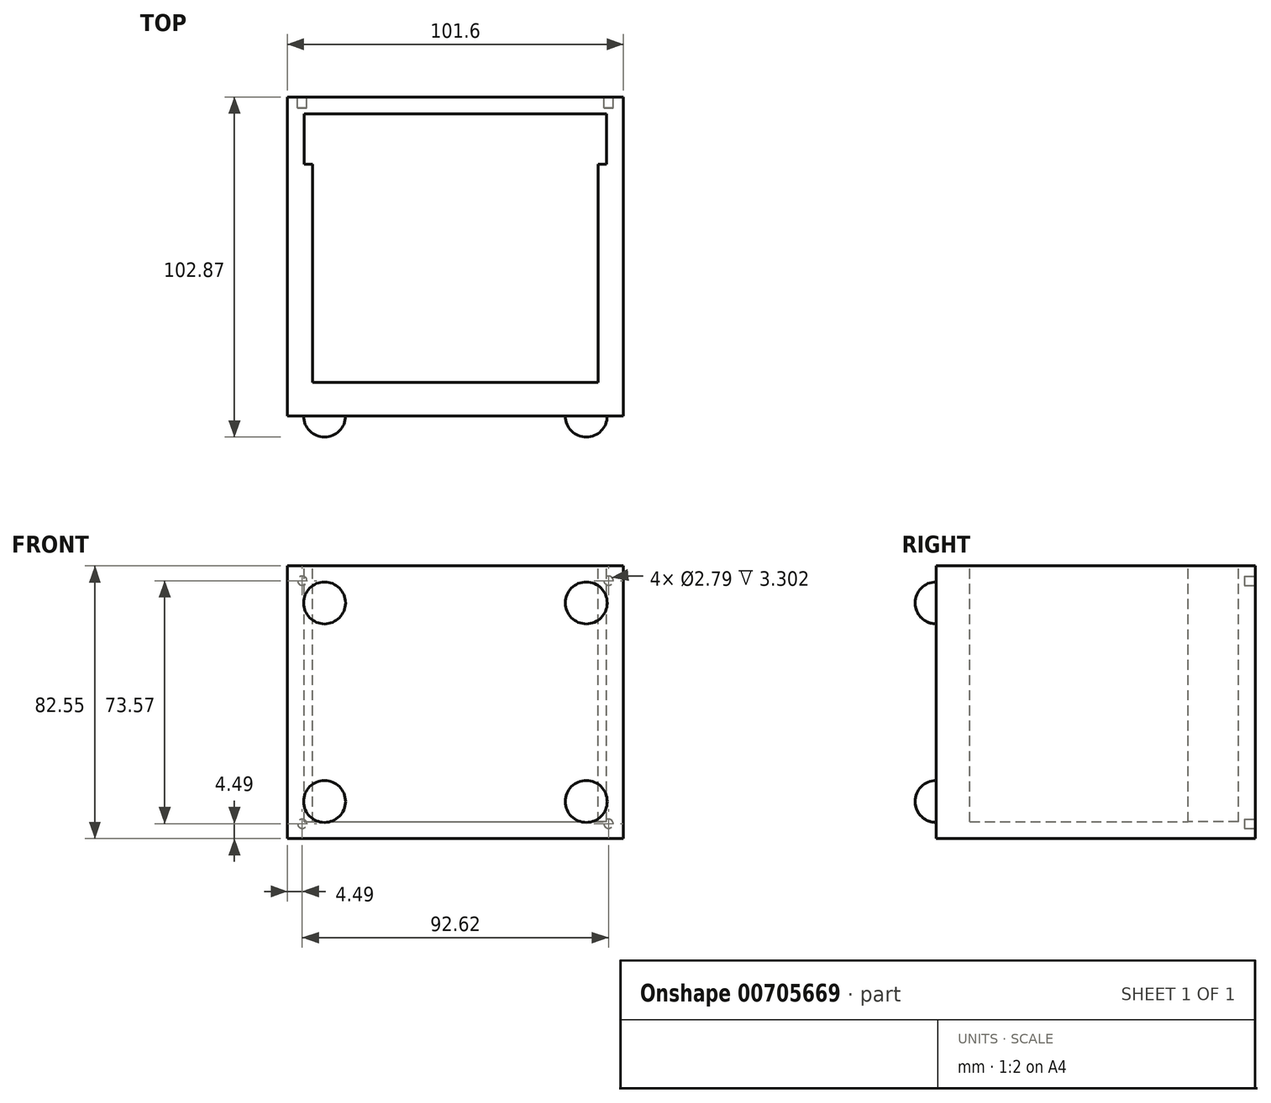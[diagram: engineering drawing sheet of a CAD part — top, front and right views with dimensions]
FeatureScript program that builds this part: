
annotation { "Feature Type Name" : "Feature", "Feature Type Description" : "" }
export const myFeature = defineFeature(function(context is Context, id is Id, definition is map)
    precondition{}
    {
        {
            var Q0;
            Q0=qCreatedBy(makeId("Top.planeOp"),FACE);
            var sketch = newSketch(context, id + "F0", { "sketchPlane" : qUnion([Q0])});
            skLineSegment(sketch, "E0.bottom", {"start": v(-50.8, 48.26) * mm, "end": v(50.8, 48.26) * mm});
            skLineSegment(sketch, "E0.top", {"start": v(-50.8, -48.26) * mm, "end": v(50.8, -48.26) * mm});
            skLineSegment(sketch, "E0.left", {"start": v(-50.8, 48.26) * mm, "end": v(-50.8, -48.26) * mm});
            skLineSegment(sketch, "E0.right", {"start": v(50.8, 48.26) * mm, "end": v(50.8, -48.26) * mm});
            skPoint(sketch, "E0.middle", {"position": v(0, 0) * mm});
            skSolve(sketch);
        }
        {
            var Q0;
            Q0 = qSketchRegion(id + "F0", true);
            extrude(context, id + "F1", {"entities" : qUnion([Q0]), "depth" : 82.55 * mm, "offsetDistance" : 25.4 * mm});
        }
        {
            var Q0;
            Q0=makeQuery(id+"F1.opExtrude","CAP_FACE",FACE,{"disambiguationData":[OSD([sQuery(id+"F0.wireOp",EDGE,"E0.bottom"),sQuery(id+"F0.wireOp",EDGE,"E0.top"),sQuery(id+"F0.wireOp",EDGE,"E0.left"),sQuery(id+"F0.wireOp",EDGE,"E0.right")])],"isStart":false});
            var sketch = newSketch(context, id + "F2", { "sketchPlane" : qUnion([Q0])});
            skLineSegment(sketch, "E1.bottom", {"start": v(-45.72, 43.18) * mm, "end": v(45.72, 43.18) * mm});
            skLineSegment(sketch, "E1.top", {"start": v(-45.72, -38.1) * mm, "end": v(45.72, -38.1) * mm});
            skLineSegment(sketch, "E1.left", {"start": v(-45.72, 43.18) * mm, "end": v(-45.72, -38.1) * mm});
            skLineSegment(sketch, "E1.right", {"start": v(45.72, 43.18) * mm, "end": v(45.72, -38.1) * mm});
            skSolve(sketch);
        }
        {
            var Q0;
            Q0 = qSketchRegion(id + "F2", true);
            extrude(context, id + "F3", {"entities" : qUnion([Q0]), "operationType" : NewBodyOperationType.REMOVE, "oppositeDirection" : true, "depth" : 77.47 * mm, "offsetDistance" : 25.4 * mm});
        }
        {
            var Q0;
            Q0=makeQuery(id+"F1.opExtrude","CAP_FACE",FACE,{"disambiguationData":[OSD([sQuery(id+"F0.wireOp",EDGE,"E0.bottom"),sQuery(id+"F0.wireOp",EDGE,"E0.top"),sQuery(id+"F0.wireOp",EDGE,"E0.left"),sQuery(id+"F0.wireOp",EDGE,"E0.right")])],"isStart":false});
            var sketch = newSketch(context, id + "F4", { "sketchPlane" : qUnion([Q0])});
            skLineSegment(sketch, "E2.bottom", {"start": v(-45.72, -38.1) * mm, "end": v(-43.18, -38.1) * mm});
            skLineSegment(sketch, "E2.top", {"start": v(-45.72, 27.94) * mm, "end": v(-43.18, 27.94) * mm});
            skLineSegment(sketch, "E2.left", {"start": v(-45.72, -38.1) * mm, "end": v(-45.72, 27.94) * mm});
            skLineSegment(sketch, "E2.right", {"start": v(-43.18, -38.1) * mm, "end": v(-43.18, 27.94) * mm});
            skLineSegment(sketch, "E3.bottom", {"start": v(45.72, -38.1) * mm, "end": v(43.18, -38.1) * mm});
            skLineSegment(sketch, "E3.top", {"start": v(45.72, 27.94) * mm, "end": v(43.18, 27.94) * mm});
            skLineSegment(sketch, "E3.left", {"start": v(45.72, -38.1) * mm, "end": v(45.72, 27.94) * mm});
            skLineSegment(sketch, "E3.right", {"start": v(43.18, -38.1) * mm, "end": v(43.18, 27.94) * mm});
            skSolve(sketch);
        }
        {
            var Q0;
            Q0 = qSketchRegion(id + "F4", true);
            extrude(context, id + "F5", {"entities" : qUnion([Q0]), "operationType" : NewBodyOperationType.ADD, "oppositeDirection" : true, "depth" : 81.28 * mm, "offsetDistance" : 25.4 * mm});
        }
        {
            var Q0;
            Q0=makeQuery(id+"F1.opExtrude","SWEPT_FACE",FACE,{"disambiguationData":[OSD([sQuery(id+"F0.wireOp",EDGE,"E0.bottom")])]});
            var sketch = newSketch(context, id + "F6", { "sketchPlane" : qUnion([Q0])});
            skCircle(sketch, "E4", {"center": v(-46.3, 78.06) * mm, "radius": 1.4 * mm});
            skCircle(sketch, "E5", {"center": v(46.3, 78.06) * mm, "radius": 1.4 * mm});
            skCircle(sketch, "E6", {"center": v(46.3, 4.5) * mm, "radius": 1.4 * mm});
            skCircle(sketch, "E7", {"center": v(-46.3, 4.5) * mm, "radius": 1.4 * mm});
            skSolve(sketch);
        }
        {
            var Q0;
            Q0 = qSketchRegion(id + "F6", true);
            extrude(context, id + "F7", {"entities" : qUnion([Q0]), "operationType" : NewBodyOperationType.REMOVE, "oppositeDirection" : true, "depth" : 3.3 * mm, "offsetDistance" : 25.4 * mm});
        }
        {
            var Q0;
            Q0=makeQuery(id+"F1.opExtrude","SWEPT_FACE",FACE,{"disambiguationData":[OSD([sQuery(id+"F0.wireOp",EDGE,"E0.top")])]});
            var sketch = newSketch(context, id + "F8", { "sketchPlane" : qUnion([Q0])});
            skLineSegment(sketch, "E8", {"start": v(-50.8, 82.55) * mm, "end": v(-39.57, 71.32) * mm});
            skLineSegment(sketch, "E9", {"start": v(50.8, 82.55) * mm, "end": v(39.57, 71.32) * mm});
            skLineSegment(sketch, "E10", {"start": v(-50.8, 0) * mm, "end": v(-39.57, 11.23) * mm});
            skLineSegment(sketch, "E11", {"start": v(50.8, 0) * mm, "end": v(39.57, 11.23) * mm});
            skCircle(sketch, "E12", {"center": v(-39.57, 71.32) * mm, "radius": 6.35 * mm});
            skCircle(sketch, "E13", {"center": v(39.57, 71.32) * mm, "radius": 6.35 * mm});
            skCircle(sketch, "E14", {"center": v(39.57, 11.23) * mm, "radius": 6.35 * mm});
            skCircle(sketch, "E15", {"center": v(-39.57, 11.23) * mm, "radius": 6.35 * mm});
            skSolve(sketch);
        }
        {
            var Q0;
            Q0 = qSketchRegion(id + "F8", true);
            extrude(context, id + "F9", {"entities" : qUnion([Q0]), "operationType" : NewBodyOperationType.ADD, "depth" : 6.35 * mm, "offsetDistance" : 25.4 * mm});
        }
        {
            var Q0;
            Q0=makeQuery(id+"F9.opExtrude","CAP_EDGE",EDGE,{"disambiguationData":[OSD([sQuery(id+"F8.wireOp",EDGE,"E12")])],"isStart":false});
            var Q1;
            Q1=makeQuery(id+"F9.opExtrude","CAP_FACE",FACE,{"disambiguationData":[OSD([sQuery(id+"F8.wireOp",EDGE,"E13")])],"isStart":false});
            var Q2;
            Q2=makeQuery(id+"F9.opExtrude","CAP_FACE",FACE,{"disambiguationData":[OSD([sQuery(id+"F8.wireOp",EDGE,"E14")])],"isStart":false});
            var Q3;
            Q3=makeQuery(id+"F9.opExtrude","CAP_FACE",FACE,{"disambiguationData":[OSD([sQuery(id+"F8.wireOp",EDGE,"E15")])],"isStart":false});
            fillet(context, id + "F10", {"entities" : qUnion([Q0, Q1, Q2, Q3]), "radius" : 6.35 * mm, "tangentPropagation" : true, "allowEdgeOverflow" : false});
        }
    });
